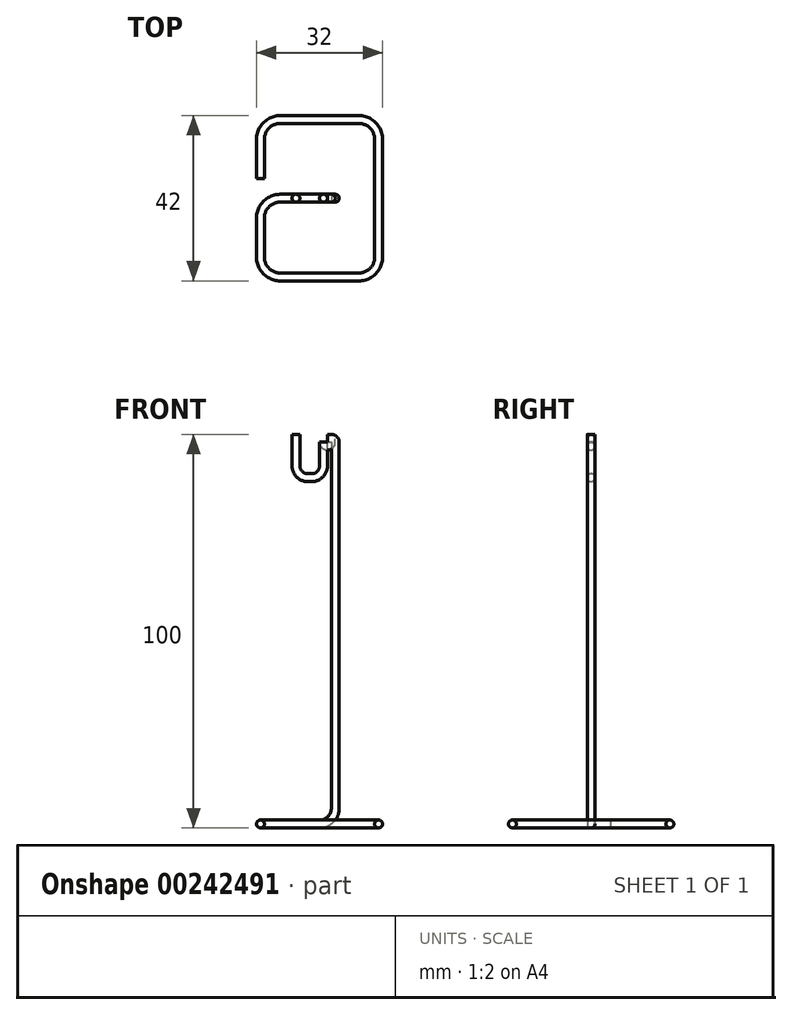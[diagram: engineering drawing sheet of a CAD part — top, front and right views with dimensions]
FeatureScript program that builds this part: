
annotation { "Feature Type Name" : "Feature", "Feature Type Description" : "" }
export const myFeature = defineFeature(function(context is Context, id is Id, definition is map)
    precondition{}
    {
        {
            var Q0;
            Q0=qCreatedBy(makeId("Front.planeOp"),FACE);
            var sketch = newSketch(context, id + "F0", { "sketchPlane" : qUnion([Q0])});
            skLineSegment(sketch, "E0", {"start": v(-10, 100) * mm, "end": v(-10, 92) * mm});
            skLineSegment(sketch, "E1", {"start": v(-5, 92) * mm, "end": v(-5, 98) * mm});
            skLineSegment(sketch, "E2", {"start": v(-7, 90) * mm, "end": v(-8, 90) * mm});
            skLineSegment(sketch, "E3", {"start": v(-3, 100) * mm, "end": v(-2, 100) * mm});
            skLineSegment(sketch, "E4", {"start": v(0, 98) * mm, "end": v(0, 5) * mm});
            skLineSegment(sketch, "E5", {"start": v(-5, 0) * mm, "end": v(-5, 0) * mm});
            skPoint(sketch, "E6.visualSharp", {"position": v(-10, 90) * mm});
            skArc(sketch, "E6.filletArc", {"start": v(-10, 92) * mm, "mid": v(-9.41, 90.59) * mm, "end": v(-8, 90) * mm});
            skPoint(sketch, "E7.visualSharp", {"position": v(-5, 90) * mm});
            skArc(sketch, "E7.filletArc", {"start": v(-7, 90) * mm, "mid": v(-5.59, 90.59) * mm, "end": v(-5, 92) * mm});
            skPoint(sketch, "E8.visualSharp", {"position": v(-5, 100) * mm});
            skArc(sketch, "E8.filletArc", {"start": v(-3, 100) * mm, "mid": v(-4.41, 99.41) * mm, "end": v(-5, 98) * mm});
            skPoint(sketch, "E9.visualSharp", {"position": v(0, 100) * mm});
            skArc(sketch, "E9.filletArc", {"start": v(0, 98) * mm, "mid": v(-0.59, 99.41) * mm, "end": v(-2, 100) * mm});
            skPoint(sketch, "E10.visualSharp", {"position": v(0, 0) * mm});
            skArc(sketch, "E10.filletArc", {"start": v(-5, 0) * mm, "mid": v(-1.46, 1.46) * mm, "end": v(0, 5) * mm});
            skLineSegment(sketch, "E11", {"start": v(-5, 0) * mm, "end": v(-15, 0) * mm});
            skSolve(sketch);
        }
        {
            var Q0;
            Q0=qCreatedBy(makeId("Top.planeOp"),FACE);
            var Q1;
            Q1=sQuery(id+"F0.wireOp",VERTEX,"E0.start");
            cPlane(context, id + "F1", {"entities" : qUnion([Q0, Q1]), "cplaneType" : CPlaneType.PLANE_POINT, "offset" : 25 * mm, "width" : 150 * mm, "height" : 150 * mm});
        }
        {
            var Q0;
            Q0=qCreatedBy(id+"F1.planeOp",FACE);
            var sketch = newSketch(context, id + "F2", { "sketchPlane" : qUnion([Q0])});
            skCircle(sketch, "E12", {"center": v(-11, 0) * mm, "radius": 1 * mm});
            skSolve(sketch);
        }
        {
            var Q0;
            Q0=qCreatedBy(makeId("Top.planeOp"),FACE);
            var sketch = newSketch(context, id + "F3", { "sketchPlane" : qUnion([Q0])});
            skLineSegment(sketch, "E13", {"start": v(-20, 5) * mm, "end": v(-20, 15) * mm});
            skLineSegment(sketch, "E14", {"start": v(5, 20) * mm, "end": v(-15, 20) * mm});
            skLineSegment(sketch, "E15", {"start": v(10, 15) * mm, "end": v(10, -15) * mm});
            skLineSegment(sketch, "E16", {"start": v(5, -20) * mm, "end": v(-15, -20) * mm});
            skLineSegment(sketch, "E17", {"start": v(-20, -5) * mm, "end": v(-20, -15) * mm});
            skLineSegment(sketch, "E18", {"start": v(-15, 0) * mm, "end": v(-15, 0) * mm});
            skPoint(sketch, "E19.visualSharp", {"position": v(-20, 20) * mm});
            skArc(sketch, "E19.filletArc", {"start": v(-15, 20) * mm, "mid": v(-18.54, 18.54) * mm, "end": v(-20, 15) * mm});
            skPoint(sketch, "E20.visualSharp", {"position": v(10, 20) * mm});
            skArc(sketch, "E20.filletArc", {"start": v(10, 15) * mm, "mid": v(8.54, 18.54) * mm, "end": v(5, 20) * mm});
            skPoint(sketch, "E21.visualSharp", {"position": v(10, -20) * mm});
            skArc(sketch, "E21.filletArc", {"start": v(5, -20) * mm, "mid": v(8.54, -18.54) * mm, "end": v(10, -15) * mm});
            skPoint(sketch, "E22.visualSharp", {"position": v(-20, -20) * mm});
            skArc(sketch, "E22.filletArc", {"start": v(-20, -15) * mm, "mid": v(-18.54, -18.54) * mm, "end": v(-15, -20) * mm});
            skPoint(sketch, "E23.visualSharp", {"position": v(-20, 0) * mm});
            skArc(sketch, "E23.filletArc", {"start": v(-15, 0) * mm, "mid": v(-18.54, -1.46) * mm, "end": v(-20, -5) * mm});
            skSolve(sketch);
        }
        {
            var Q0;
            Q0=makeQuery(id+"F2.imprint","IMPRINT",FACE,{"disambiguationData":[TD([[makeQuery(id+"F2.imprint","IMPRINT",EDGE,{"derivedFrom":sQuery(id+"F2.wireOp",EDGE,"E12")}),1.0]])]});
            var Q1;
            Q1=sQuery(id+"F0.wireOp",EDGE,"E0");
            var Q2;
            Q2=sQuery(id+"F0.wireOp",EDGE,"E6.filletArc");
            var Q3;
            Q3=sQuery(id+"F0.wireOp",EDGE,"E2");
            var Q4;
            Q4=sQuery(id+"F0.wireOp",EDGE,"E7.filletArc");
            var Q5;
            Q5=sQuery(id+"F0.wireOp",EDGE,"E1");
            var Q6;
            Q6=sQuery(id+"F0.wireOp",EDGE,"E8.filletArc");
            var Q7;
            Q7=sQuery(id+"F0.wireOp",EDGE,"E3");
            var Q8;
            Q8=sQuery(id+"F0.wireOp",EDGE,"E9.filletArc");
            var Q9;
            Q9=sQuery(id+"F0.wireOp",EDGE,"E4");
            var Q10;
            Q10=sQuery(id+"F0.wireOp",EDGE,"E10.filletArc");
            var Q11;
            Q11=sQuery(id+"F0.wireOp",EDGE,"E11");
            var Q12;
            Q12=sQuery(id+"F3.wireOp",EDGE,"E23.filletArc");
            var Q13;
            Q13=sQuery(id+"F3.wireOp",EDGE,"E17");
            var Q14;
            Q14=sQuery(id+"F3.wireOp",EDGE,"E22.filletArc");
            var Q15;
            Q15=sQuery(id+"F3.wireOp",EDGE,"E16");
            var Q16;
            Q16=sQuery(id+"F3.wireOp",EDGE,"E21.filletArc");
            var Q17;
            Q17=sQuery(id+"F3.wireOp",EDGE,"E15");
            var Q18;
            Q18=sQuery(id+"F3.wireOp",EDGE,"E20.filletArc");
            var Q19;
            Q19=sQuery(id+"F3.wireOp",EDGE,"E14");
            var Q20;
            Q20=sQuery(id+"F3.wireOp",EDGE,"E19.filletArc");
            var Q21;
            Q21=sQuery(id+"F3.wireOp",EDGE,"E13");
            sweep(context, id + "F4", {"profiles" : qUnion([Q0]), "path" : qUnion([Q1, Q2, Q3, Q4, Q5, Q6, Q7, Q8, Q9, Q10, Q11, Q12, Q13, Q14, Q15, Q16, Q17, Q18, Q19, Q20, Q21])});
        }
    });
